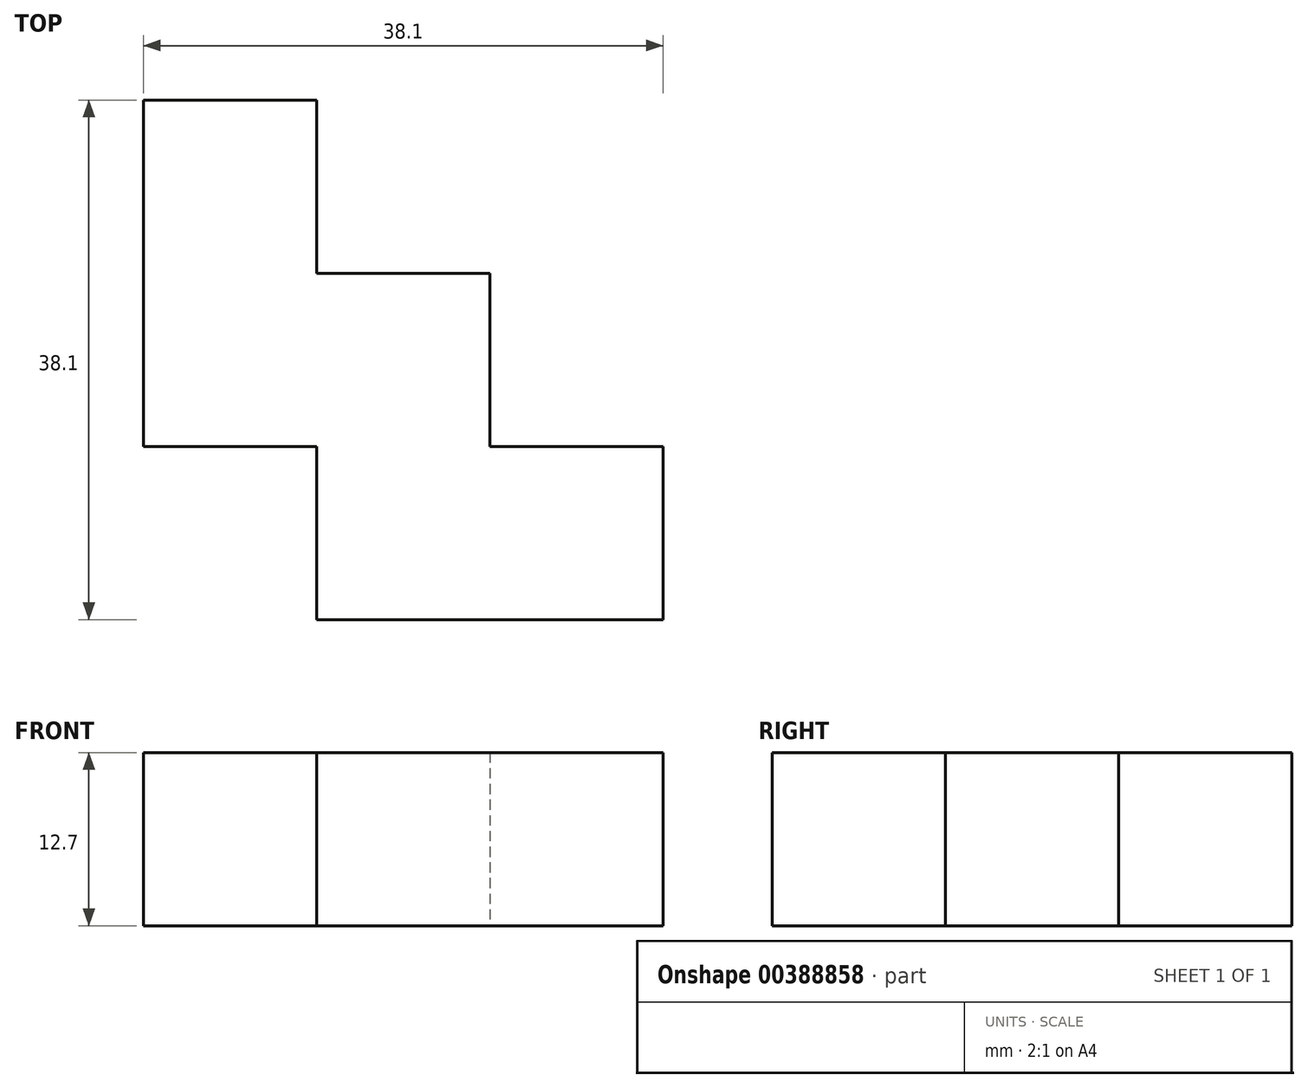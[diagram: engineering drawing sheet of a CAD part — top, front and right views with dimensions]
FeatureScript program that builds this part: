
annotation { "Feature Type Name" : "Feature", "Feature Type Description" : "" }
export const myFeature = defineFeature(function(context is Context, id is Id, definition is map)
    precondition{}
    {
        {
            var Q0;
            Q0=qCreatedBy(makeId("Top.planeOp"),FACE);
            var sketch = newSketch(context, id + "F0", { "sketchPlane" : qUnion([Q0])});
            skLineSegment(sketch, "E0.top", {"start": v(0, 12.7) * mm, "end": v(-12.7, 12.7) * mm});
            skLineSegment(sketch, "E0.left", {"start": v(0, 0) * mm, "end": v(0, 12.7) * mm});
            skLineSegment(sketch, "E0.right", {"start": v(-12.7, 0) * mm, "end": v(-12.7, 12.7) * mm});
            skPoint(sketch, "E1.oppositeSnap0", {"position": v(-12.7, 6.35) * mm});
            skLineSegment(sketch, "E1.top", {"start": v(0, -12.7) * mm, "end": v(-12.7, -12.7) * mm});
            skLineSegment(sketch, "E1.right", {"start": v(-12.7, 0) * mm, "end": v(-12.7, -12.7) * mm});
            skLineSegment(sketch, "E2.bottom", {"start": v(0, 0) * mm, "end": v(12.7, 0) * mm});
            skLineSegment(sketch, "E2.right", {"start": v(12.7, 0) * mm, "end": v(12.7, -12.7) * mm});
            skLineSegment(sketch, "E3.top", {"start": v(0, -25.4) * mm, "end": v(12.7, -25.4) * mm});
            skLineSegment(sketch, "E3.left", {"start": v(0, -12.7) * mm, "end": v(0, -25.4) * mm});
            skLineSegment(sketch, "E4.bottom", {"start": v(12.7, -12.7) * mm, "end": v(25.4, -12.7) * mm});
            skLineSegment(sketch, "E4.top", {"start": v(12.7, -25.4) * mm, "end": v(25.4, -25.4) * mm});
            skLineSegment(sketch, "E4.right", {"start": v(25.4, -12.7) * mm, "end": v(25.4, -25.4) * mm});
            skSolve(sketch);
        }
        {
            var Q0;
            Q0=makeQuery(id+"F0.imprint","IMPRINT",FACE,{"disambiguationData":[TD([[makeQuery(id+"F0.imprint","IMPRINT",EDGE,{"derivedFrom":sQuery(id+"F0.wireOp",EDGE,"E0.top")}),1.0]])]});
            extrude(context, id + "F1", {"entities" : qUnion([Q0]), "depth" : 12.7 * mm});
        }
    });
